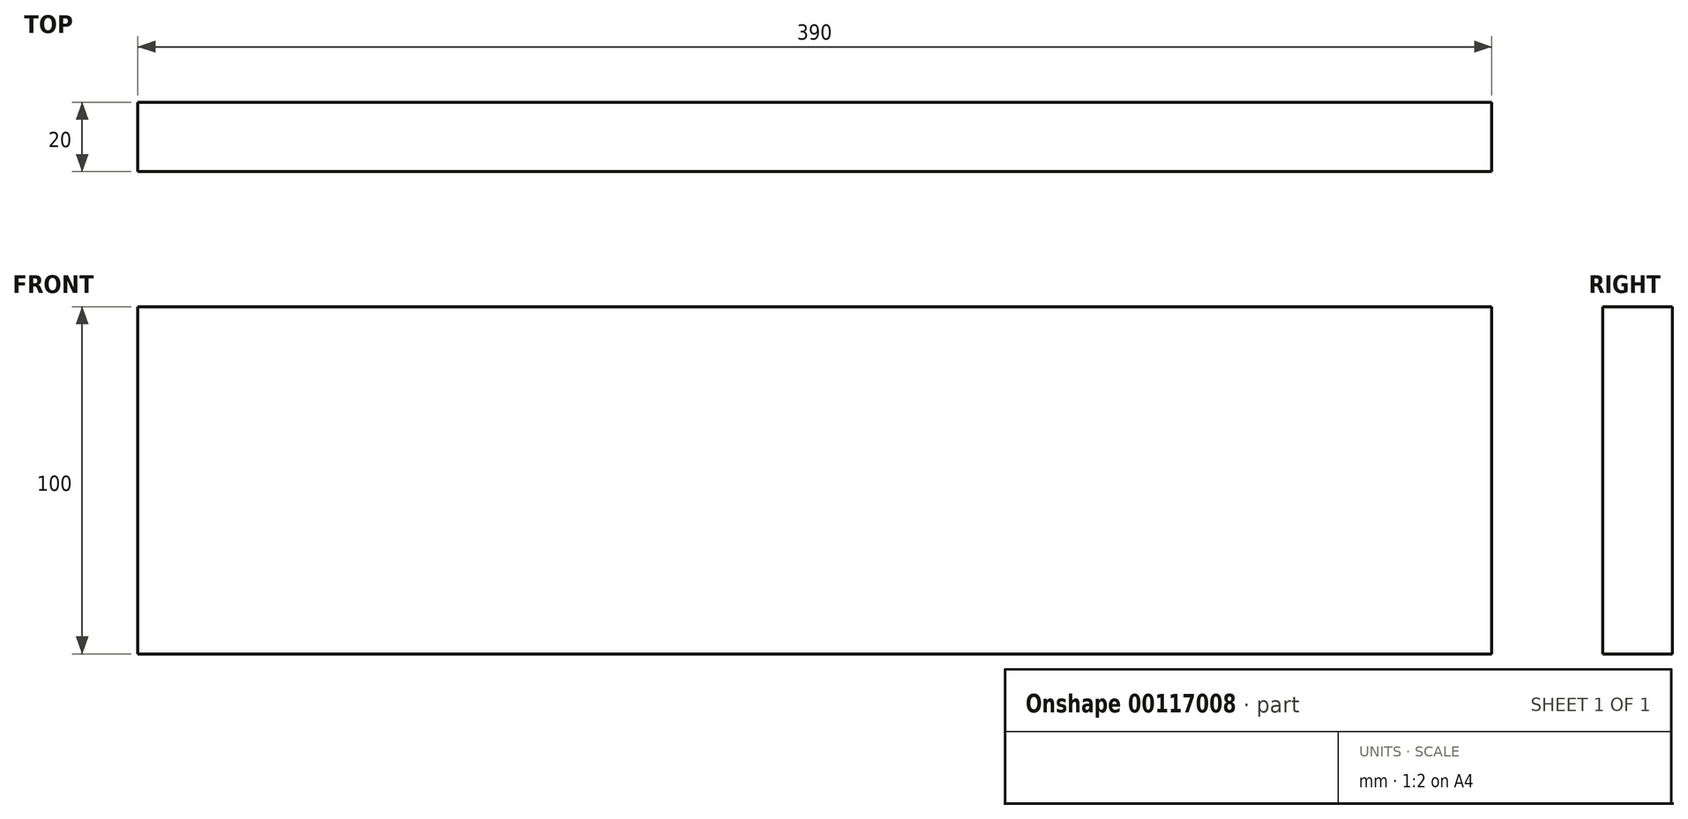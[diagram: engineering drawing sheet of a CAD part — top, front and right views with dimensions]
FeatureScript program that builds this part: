
annotation { "Feature Type Name" : "Feature", "Feature Type Description" : "" }
export const myFeature = defineFeature(function(context is Context, id is Id, definition is map)
    precondition{}
    {
        {
            var Q0;
            Q0=qCreatedBy(makeId("Top.planeOp"),FACE);
            var sketch = newSketch(context, id + "F0", { "sketchPlane" : qUnion([Q0])});
            skLineSegment(sketch, "E0.bottom", {"start": v(-68.57, 54.14) * mm, "end": v(321.43, 54.14) * mm});
            skLineSegment(sketch, "E0.top", {"start": v(-68.57, 34.14) * mm, "end": v(321.43, 34.14) * mm});
            skLineSegment(sketch, "E0.left", {"start": v(-68.57, 54.14) * mm, "end": v(-68.57, 34.14) * mm});
            skLineSegment(sketch, "E0.right", {"start": v(321.43, 54.14) * mm, "end": v(321.43, 34.14) * mm});
            skSolve(sketch);
        }
        {
            var Q0;
            Q0=makeQuery(id+"F0.imprint","IMPRINT",FACE,{"disambiguationData":[TD([[makeQuery(id+"F0.imprint","IMPRINT",EDGE,{"derivedFrom":sQuery(id+"F0.wireOp",EDGE,"E0.bottom")}),-1.0]])]});
            extrude(context, id + "F1", {"entities" : qUnion([Q0]), "depth" : 100 * mm, "offsetDistance" : 25 * mm});
        }
    });
